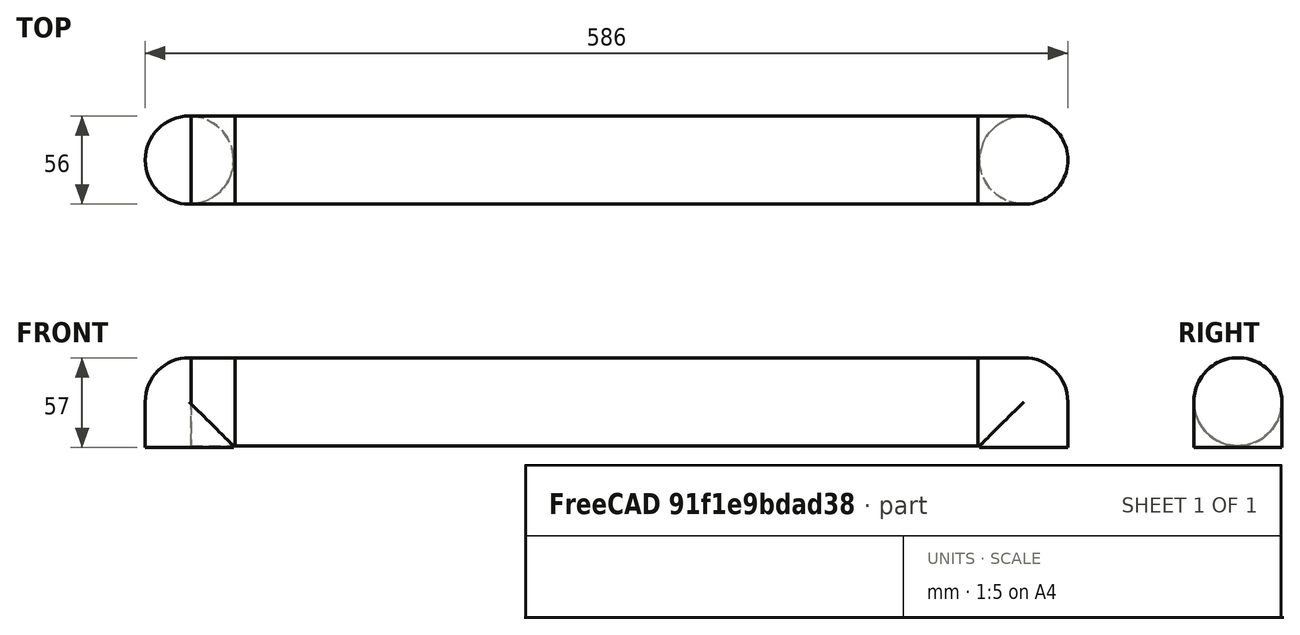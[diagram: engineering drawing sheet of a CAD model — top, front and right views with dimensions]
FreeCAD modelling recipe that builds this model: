
FCSTD DOCUMENT  (FreeCAD 0.21R33668 +26 (Git))
Label: arm-L2
License: All rights reserved
LicenseURL: http://en.wikipedia.org/wiki/All_rights_reserved
objects: App::FeaturePython×4, Part::FeaturePython×2, Part::Cylinder×1, App::Part×1
note: 3 computed .brp shape members not serialized (recipe doc carries the construction recipe); baked Part::Feature solids carry a one-line shape summary decoded from their .brp

FEATURE [Part::FeaturePython] b_arm_subpart_angle_001_  label="arm-subpart-angle_001"  # a2plus imported part (geometry in sourceFile) (typed FeaturePython)
  Placement = pos=(28,0,0) rot=(0,1,0;3.14159rad)
  a2p_Version = 0.4.60i
  fixedPosition = true
  objectType = a2pPart
  sourceFile = .\arm-subpart-angle.FCStd
  subassemblyImport = false
  timeLastImport = 1.69953e+09
  updateColors = true
FEATURE [Part::Cylinder] Cylinder
  Angle = 360
  AttacherType = Attacher::AttachEngine3D
  FirstAngle = 0
  Height = 500
  Placement = pos=(1,-4e-16,-4.1e-15) rot=(0,1,0;1.5708rad)
  Radius = 28
  SecondAngle = 0
FEATURE [Part::FeaturePython] b_arm_subpart_angle_001_001  label="arm-subpart-angle_002"  # a2plus imported part (geometry in sourceFile) (typed FeaturePython)
  Placement = pos=(502,-2.04617e-06,5.12029e-05) rot=(1,0,0;3.14159rad)
  a2p_Version = 0.4.60i
  fixedPosition = false
  objectType = a2pPart
  sourceFile = .\arm-subpart-angle.FCStd
  subassemblyImport = false
  timeLastImport = 1.69953e+09
  updateColors = true
FEATURE [App::Part] Part
  Group = -> [b_arm_subpart_angle_001_,Cylinder,b_arm_subpart_angle_001_001]
  Origin = -> Origin
FEATURE [App::FeaturePython] centerOfMass_001  label="centerOfMass_001__Cylinder"  # a2plus constraint (typed FeaturePython)
  Object1 = b_arm_subpart_angle_001_
  Object2 = Cylinder
  ParentTreeObject = -> b_arm_subpart_angle_001_
  SubElement1 = Face5
  SubElement2 = Face2
  Suppressed = false
  Type = CenterOfMass
  directionConstraint = 0
  lockRotation = true
  offset = 0
FEATURE [App::FeaturePython] centerOfMass_001_mirror  label="centerOfMass_001__arm-subpart-angle_001"  # a2plus constraint (typed FeaturePython)
  Object1 = b_arm_subpart_angle_001_
  Object2 = Cylinder
  ParentTreeObject = -> Cylinder
  SubElement1 = Face5
  SubElement2 = Face2
  Suppressed = false
  Type = CenterOfMass
  directionConstraint = 0
  lockRotation = true
  offset = 0
FEATURE [App::FeaturePython] centerOfMass_002  label="centerOfMass_002__arm-subpart-angle_002"  # a2plus constraint (typed FeaturePython)
  Object1 = Cylinder
  Object2 = b_arm_subpart_angle_001_001
  ParentTreeObject = -> Cylinder
  SubElement1 = Face3
  SubElement2 = Face5
  Suppressed = false
  Type = CenterOfMass
  directionConstraint = 1
  lockRotation = true
  offset = 0
FEATURE [App::FeaturePython] centerOfMass_002_mirror  label="centerOfMass_002__Cylinder"  # a2plus constraint (typed FeaturePython)
  Object1 = Cylinder
  Object2 = b_arm_subpart_angle_001_001
  ParentTreeObject = -> b_arm_subpart_angle_001_001
  SubElement1 = Face3
  SubElement2 = Face5
  Suppressed = false
  Type = CenterOfMass
  directionConstraint = 1
  lockRotation = true
  offset = 0
